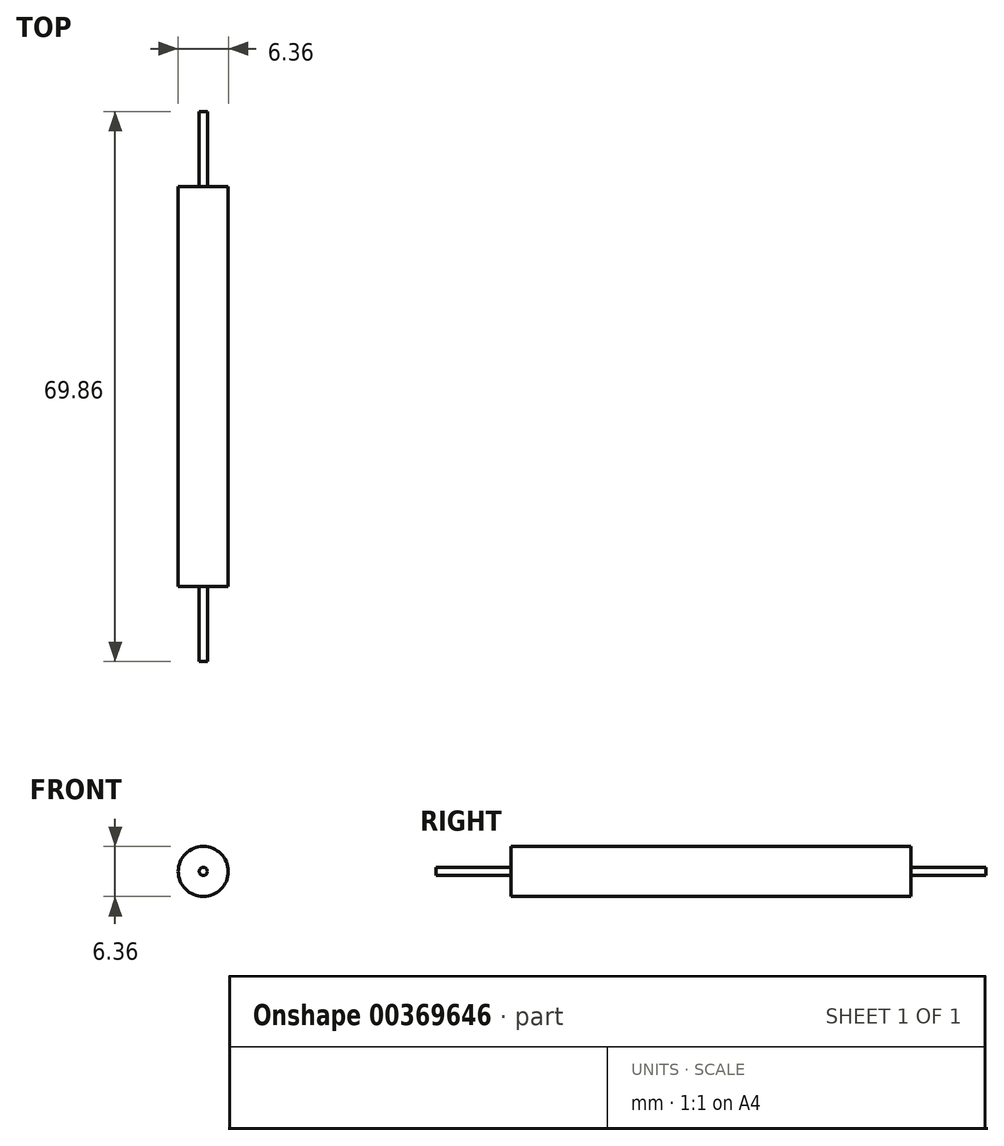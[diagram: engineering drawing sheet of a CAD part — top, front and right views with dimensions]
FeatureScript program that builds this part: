
annotation { "Feature Type Name" : "Feature", "Feature Type Description" : "" }
export const myFeature = defineFeature(function(context is Context, id is Id, definition is map)
    precondition{}
    {
        {
            assignVariable(context, id + "F0", {"name" : "AxleLength", "anyValue" : 9.52 * mm});
        }
        {
            assignVariable(context, id + "F1", {"name" : "RollerLength", "anyValue" : 50.8 * mm});
        }
        {
            var Q0;
            Q0=qCreatedBy(makeId("Front.planeOp"),FACE);
            var sketch = newSketch(context, id + "F2", { "sketchPlane" : qUnion([Q0])});
            skCircle(sketch, "E0", {"center": v(0, 0) * mm, "radius": 3.18 * mm});
            skSolve(sketch);
        }
        {
            var Q0;
            Q0=qCreatedBy(makeId("Front.planeOp"),FACE);
            var sketch = newSketch(context, id + "F3", { "sketchPlane" : qUnion([Q0])});
            skCircle(sketch, "E1", {"center": v(0, 0) * mm, "radius": 0.51 * mm});
            skSolve(sketch);
        }
        {
            var Q0;
            Q0=qCreatedBy(makeId("Front.planeOp"),FACE);
            var sketch = newSketch(context, id + "F4", { "sketchPlane" : qUnion([Q0])});
            skCircle(sketch, "E2", {"center": v(0, 0) * mm, "radius": 0.51 * mm});
            skSolve(sketch);
        }
        {
            var Q0;
            Q0 = qSketchRegion(id + "F2", true);
            extrude(context, id + "F5", {"entities" : qUnion([Q0]), "depth" : getVariable(context, 'RollerLength')});
        }
        {
            var Q0;
            Q0 = qSketchRegion(id + "F3", true);
            extrude(context, id + "F6", {"entities" : qUnion([Q0]), "operationType" : NewBodyOperationType.ADD, "oppositeDirection" : true, "depth" : getVariable(context, 'AxleLength')});
        }
        {
            var Q0;
            Q0 = qSketchRegion(id + "F4", true);
            extrude(context, id + "F7", {"entities" : qUnion([Q0]), "operationType" : NewBodyOperationType.ADD, "depth" : getVariable(context, 'AxleLength') + getVariable(context, 'RollerLength')});
        }
    });
